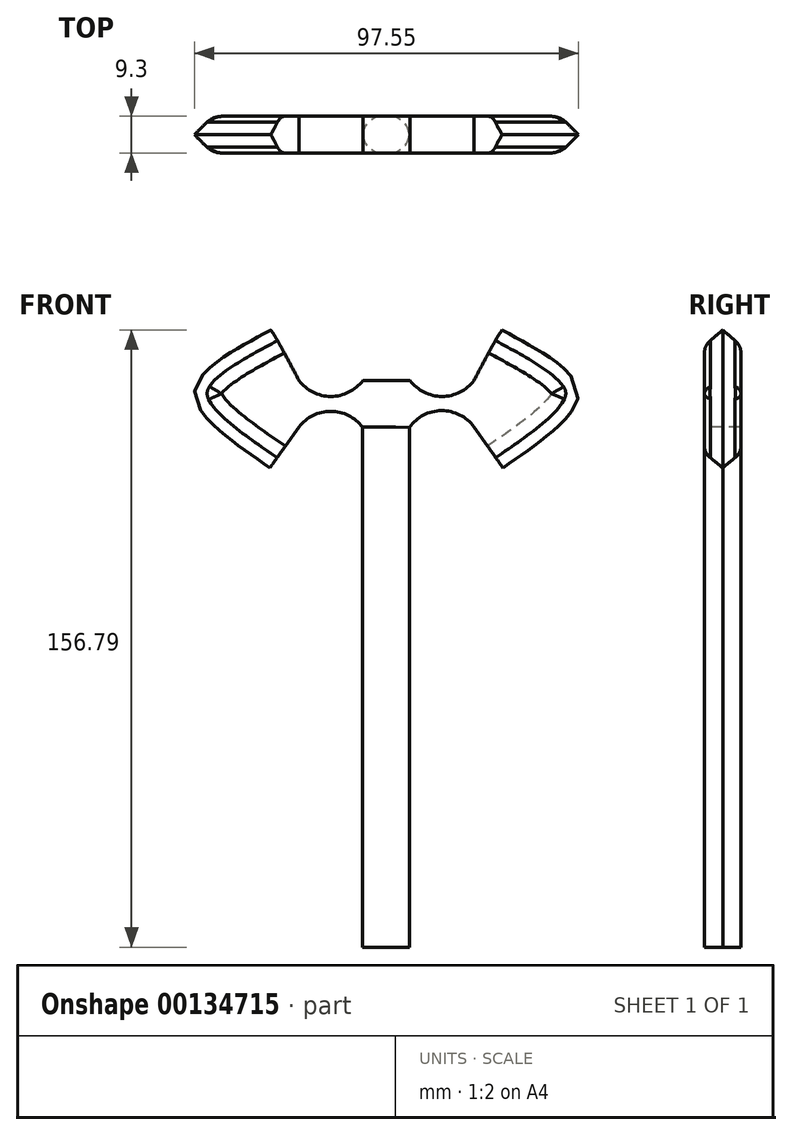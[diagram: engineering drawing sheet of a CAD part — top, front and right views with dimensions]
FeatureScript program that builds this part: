
annotation { "Feature Type Name" : "Feature", "Feature Type Description" : "" }
export const myFeature = defineFeature(function(context is Context, id is Id, definition is map)
    precondition{}
    {
        {
            var Q0;
            Q0=qCreatedBy(makeId("Front.planeOp"),FACE);
            var sketch = newSketch(context, id + "F0", { "sketchPlane" : qUnion([Q0])});
            skLineSegment(sketch, "E0", {"start": v(-59.33, 62.86) * mm, "end": v(-59.33, -69.24) * mm});
            skLineSegment(sketch, "E1", {"start": v(-59.33, -69.24) * mm, "end": v(-47.38, -69.24) * mm});
            skLineSegment(sketch, "E2", {"start": v(-47.38, -69.24) * mm, "end": v(-47.38, 62.86) * mm});
            skLineSegment(sketch, "E3", {"start": v(-47.38, 62.86) * mm, "end": v(-59.33, 62.86) * mm});
            skSolve(sketch);
        }
        {
            var Q0;
            Q0=qCreatedBy(makeId("Front.planeOp"),FACE);
            var sketch = newSketch(context, id + "F1", { "sketchPlane" : qUnion([Q0])});
            skLineSegment(sketch, "E4", {"start": v(-47.22, 74.74) * mm, "end": v(-59.23, 74.74) * mm});
            skLineSegment(sketch, "E5", {"start": v(-59.32, 62.87) * mm, "end": v(-47.4, 62.85) * mm});
            skArc(sketch, "E6", {"start": v(-47.22, 74.74) * mm, "mid": v(-39.1, 70.68) * mm, "end": v(-30.98, 74.74) * mm});
            skPoint(sketch, "E7.startSnap0", {"position": v(-47.22, 68.84) * mm});
            skPoint(sketch, "E7.startSnap1", {"position": v(-53.36, 62.86) * mm});
            skArc(sketch, "E8.MirrorCS", {"start": v(-47.4, 62.85) * mm, "mid": v(-39.21, 67.07) * mm, "end": v(-30.98, 62.95) * mm});
            skPoint(sketch, "E9.endSnap0", {"position": v(-53.22, 74.74) * mm});
            skArc(sketch, "E10.MirrorCS", {"start": v(-59.23, 74.74) * mm, "mid": v(-67.35, 70.68) * mm, "end": v(-75.46, 74.74) * mm});
            skArc(sketch, "E11.MirrorCS", {"start": v(-59.32, 62.87) * mm, "mid": v(-67.37, 66.9) * mm, "end": v(-75.46, 62.95) * mm});
            skFitSpline(sketch, "E12", {"points": [v(-30.98, 74.74) * mm, v(-23.6, 87.78) * mm, v(-23.37, 87.78) * mm], "startDerivative": vector(11.07, 21.16) * mm, "endDerivative": vector(1.7, -0.8) * mm});
            skFitSpline(sketch, "E13", {"points": [v(-23.37, 87.78) * mm, v(-4.02, 71.77) * mm, v(-23.37, 52.2) * mm], "startDerivative": vector(58.52, -31.43) * mm, "endDerivative": vector(-57.64, -39.67) * mm});
            skFitSpline(sketch, "E14", {"points": [v(-30.98, 62.95) * mm, v(-23.37, 52.2) * mm], "startDerivative": vector(7.6, -10.75) * mm, "endDerivative": vector(7.6, -10.75) * mm});
            skFitSpline(sketch, "E15.MirrorCS", {"points": [v(-75.46, 62.95) * mm, v(-83.07, 52.2) * mm], "startDerivative": vector(-7.6, -10.75) * mm, "endDerivative": vector(-7.6, -10.75) * mm});
            skFitSpline(sketch, "E16.MirrorCS", {"points": [v(-75.46, 74.74) * mm, v(-82.85, 87.78) * mm, v(-83.07, 87.78) * mm], "startDerivative": vector(-11.07, 21.16) * mm, "endDerivative": vector(-1.7, -0.8) * mm});
            skFitSpline(sketch, "E17.MirrorCS", {"points": [v(-83.07, 87.78) * mm, v(-102.42, 71.77) * mm, v(-83.07, 52.2) * mm], "startDerivative": vector(-58.52, -31.43) * mm, "endDerivative": vector(57.64, -39.67) * mm});
            skLineSegment(sketch, "E18", {"start": v(-47.22, 74.74) * mm, "end": v(-47.4, 62.85) * mm});
            skLineSegment(sketch, "E19", {"start": v(-59.23, 74.74) * mm, "end": v(-59.32, 62.87) * mm});
            skSolve(sketch);
        }
        {
            var Q0;
            Q0 = qSketchRegion(id + "F1", true);
            var Q1;
            Q1 = qSketchRegion(id + "F0", true);
            extrude(context, id + "F2", {"entities" : qUnion([Q0, Q1]), "depth" : 9.3 * mm});
        }
        {
            var Q0;
            Q0=makeQuery(id+"F2.opExtrude","CAP_EDGE",EDGE,{"disambiguationData":[OSD([sQuery(id+"F0.wireOp",EDGE,"E0")])],"isStart":false});
            var Q1;
            Q1=makeQuery(id+"F2.opExtrude","CAP_EDGE",EDGE,{"disambiguationData":[OSD([sQuery(id+"F0.wireOp",EDGE,"E2")])],"isStart":false});
            var Q2;
            Q2=makeQuery(id+"F2.opExtrude","CAP_EDGE",EDGE,{"disambiguationData":[OSD([sQuery(id+"F0.wireOp",EDGE,"E2")])],"isStart":true});
            var Q3;
            Q3=makeQuery(id+"F2.opExtrude","CAP_EDGE",EDGE,{"disambiguationData":[OSD([sQuery(id+"F0.wireOp",EDGE,"E0")])],"isStart":true});
            fillet(context, id + "F3", {"entities" : qUnion([Q0, Q1, Q2, Q3]), "radius" : 5.08 * mm, "tangentPropagation" : true, "allowEdgeOverflow" : false});
        }
        {
            var Q0;
            Q0=makeQuery(id+"F2.opExtrude","CAP_EDGE",EDGE,{"disambiguationData":[OSD([sQuery(id+"F1.wireOp",EDGE,"E17.MirrorCS")])],"isStart":true});
            var Q1;
            Q1=makeQuery(id+"F2.opExtrude","CAP_EDGE",EDGE,{"disambiguationData":[OSD([sQuery(id+"F1.wireOp",EDGE,"E17.MirrorCS")])],"isStart":false});
            var Q2;
            Q2=makeQuery(id+"F2.opExtrude","CAP_EDGE",EDGE,{"disambiguationData":[OSD([sQuery(id+"F1.wireOp",EDGE,"E13")])],"isStart":false});
            var Q3;
            Q3=makeQuery(id+"F2.opExtrude","CAP_EDGE",EDGE,{"disambiguationData":[OSD([sQuery(id+"F1.wireOp",EDGE,"E13")])],"isStart":true});
            chamfer(context, id + "F4", {"entities" : qUnion([Q0, Q1, Q2, Q3]), "width" : 5.08 * mm, "tangentPropagation" : true});
        }
        {
            var Q0;
            {var subQ0=sQuery(id+"F1.wireOp",EDGE,"E13");Q0=makeQuery(id+"F4.opChamfer","BLEND_EDGE",EDGE,{"blendedFrom":[makeQuery(id+"F2.opExtrude","CAP_EDGE",EDGE,{"disambiguationData":[OSD([subQ0])],"isStart":true}),makeQuery(id+"F2.opExtrude","CAP_FACE",FACE,{"disambiguationData":[OSD([sQuery(id+"F1.wireOp",EDGE,"E4"),sQuery(id+"F1.wireOp",EDGE,"E5"),sQuery(id+"F1.wireOp",EDGE,"E6"),sQuery(id+"F1.wireOp",EDGE,"E8.MirrorCS"),sQuery(id+"F1.wireOp",EDGE,"E10.MirrorCS"),sQuery(id+"F1.wireOp",EDGE,"E11.MirrorCS"),sQuery(id+"F1.wireOp",EDGE,"E12"),subQ0,sQuery(id+"F1.wireOp",EDGE,"E14"),sQuery(id+"F1.wireOp",EDGE,"E15.MirrorCS"),sQuery(id+"F1.wireOp",EDGE,"E16.MirrorCS"),sQuery(id+"F1.wireOp",EDGE,"E17.MirrorCS")])],"isStart":true})],"blendedInto":[makeQuery(id+"F2.opExtrude","CAP_FACE",FACE,{"disambiguationData":[OSD([sQuery(id+"F1.wireOp",EDGE,"E4"),sQuery(id+"F1.wireOp",EDGE,"E5"),sQuery(id+"F1.wireOp",EDGE,"E6"),sQuery(id+"F1.wireOp",EDGE,"E8.MirrorCS"),sQuery(id+"F1.wireOp",EDGE,"E10.MirrorCS"),sQuery(id+"F1.wireOp",EDGE,"E11.MirrorCS"),sQuery(id+"F1.wireOp",EDGE,"E12"),subQ0,sQuery(id+"F1.wireOp",EDGE,"E14"),sQuery(id+"F1.wireOp",EDGE,"E15.MirrorCS"),sQuery(id+"F1.wireOp",EDGE,"E16.MirrorCS"),sQuery(id+"F1.wireOp",EDGE,"E17.MirrorCS")])],"isStart":true})]});}
            var Q1;
            {var subQ0=sQuery(id+"F1.wireOp",EDGE,"E17.MirrorCS");Q1=makeQuery(id+"F4.opChamfer","BLEND_EDGE",EDGE,{"blendedFrom":[makeQuery(id+"F2.opExtrude","CAP_EDGE",EDGE,{"disambiguationData":[OSD([subQ0])],"isStart":true}),makeQuery(id+"F2.opExtrude","CAP_FACE",FACE,{"disambiguationData":[OSD([sQuery(id+"F1.wireOp",EDGE,"E4"),sQuery(id+"F1.wireOp",EDGE,"E5"),sQuery(id+"F1.wireOp",EDGE,"E6"),sQuery(id+"F1.wireOp",EDGE,"E8.MirrorCS"),sQuery(id+"F1.wireOp",EDGE,"E10.MirrorCS"),sQuery(id+"F1.wireOp",EDGE,"E11.MirrorCS"),sQuery(id+"F1.wireOp",EDGE,"E12"),sQuery(id+"F1.wireOp",EDGE,"E13"),sQuery(id+"F1.wireOp",EDGE,"E14"),sQuery(id+"F1.wireOp",EDGE,"E15.MirrorCS"),sQuery(id+"F1.wireOp",EDGE,"E16.MirrorCS"),subQ0])],"isStart":true})],"blendedInto":[makeQuery(id+"F2.opExtrude","CAP_FACE",FACE,{"disambiguationData":[OSD([sQuery(id+"F1.wireOp",EDGE,"E4"),sQuery(id+"F1.wireOp",EDGE,"E5"),sQuery(id+"F1.wireOp",EDGE,"E6"),sQuery(id+"F1.wireOp",EDGE,"E8.MirrorCS"),sQuery(id+"F1.wireOp",EDGE,"E10.MirrorCS"),sQuery(id+"F1.wireOp",EDGE,"E11.MirrorCS"),sQuery(id+"F1.wireOp",EDGE,"E12"),sQuery(id+"F1.wireOp",EDGE,"E13"),sQuery(id+"F1.wireOp",EDGE,"E14"),sQuery(id+"F1.wireOp",EDGE,"E15.MirrorCS"),sQuery(id+"F1.wireOp",EDGE,"E16.MirrorCS"),subQ0])],"isStart":true})]});}
            var Q2;
            {var subQ0=sQuery(id+"F1.wireOp",EDGE,"E13");Q2=makeQuery(id+"F4.opChamfer","BLEND_EDGE",EDGE,{"blendedFrom":[makeQuery(id+"F2.opExtrude","CAP_EDGE",EDGE,{"disambiguationData":[OSD([subQ0])],"isStart":false}),makeQuery(id+"F2.opExtrude","CAP_FACE",FACE,{"disambiguationData":[OSD([sQuery(id+"F1.wireOp",EDGE,"E4"),sQuery(id+"F1.wireOp",EDGE,"E5"),sQuery(id+"F1.wireOp",EDGE,"E6"),sQuery(id+"F1.wireOp",EDGE,"E8.MirrorCS"),sQuery(id+"F1.wireOp",EDGE,"E10.MirrorCS"),sQuery(id+"F1.wireOp",EDGE,"E11.MirrorCS"),sQuery(id+"F1.wireOp",EDGE,"E12"),subQ0,sQuery(id+"F1.wireOp",EDGE,"E14"),sQuery(id+"F1.wireOp",EDGE,"E15.MirrorCS"),sQuery(id+"F1.wireOp",EDGE,"E16.MirrorCS"),sQuery(id+"F1.wireOp",EDGE,"E17.MirrorCS")])],"isStart":false})],"blendedInto":[makeQuery(id+"F2.opExtrude","CAP_FACE",FACE,{"disambiguationData":[OSD([sQuery(id+"F1.wireOp",EDGE,"E4"),sQuery(id+"F1.wireOp",EDGE,"E5"),sQuery(id+"F1.wireOp",EDGE,"E6"),sQuery(id+"F1.wireOp",EDGE,"E8.MirrorCS"),sQuery(id+"F1.wireOp",EDGE,"E10.MirrorCS"),sQuery(id+"F1.wireOp",EDGE,"E11.MirrorCS"),sQuery(id+"F1.wireOp",EDGE,"E12"),subQ0,sQuery(id+"F1.wireOp",EDGE,"E14"),sQuery(id+"F1.wireOp",EDGE,"E15.MirrorCS"),sQuery(id+"F1.wireOp",EDGE,"E16.MirrorCS"),sQuery(id+"F1.wireOp",EDGE,"E17.MirrorCS")])],"isStart":false})]});}
            var Q3;
            {var subQ0=sQuery(id+"F1.wireOp",EDGE,"E17.MirrorCS");Q3=makeQuery(id+"F4.opChamfer","BLEND_EDGE",EDGE,{"blendedFrom":[makeQuery(id+"F2.opExtrude","CAP_EDGE",EDGE,{"disambiguationData":[OSD([subQ0])],"isStart":false}),makeQuery(id+"F2.opExtrude","CAP_FACE",FACE,{"disambiguationData":[OSD([sQuery(id+"F1.wireOp",EDGE,"E4"),sQuery(id+"F1.wireOp",EDGE,"E5"),sQuery(id+"F1.wireOp",EDGE,"E6"),sQuery(id+"F1.wireOp",EDGE,"E8.MirrorCS"),sQuery(id+"F1.wireOp",EDGE,"E10.MirrorCS"),sQuery(id+"F1.wireOp",EDGE,"E11.MirrorCS"),sQuery(id+"F1.wireOp",EDGE,"E12"),sQuery(id+"F1.wireOp",EDGE,"E13"),sQuery(id+"F1.wireOp",EDGE,"E14"),sQuery(id+"F1.wireOp",EDGE,"E15.MirrorCS"),sQuery(id+"F1.wireOp",EDGE,"E16.MirrorCS"),subQ0])],"isStart":false})],"blendedInto":[makeQuery(id+"F2.opExtrude","CAP_FACE",FACE,{"disambiguationData":[OSD([sQuery(id+"F1.wireOp",EDGE,"E4"),sQuery(id+"F1.wireOp",EDGE,"E5"),sQuery(id+"F1.wireOp",EDGE,"E6"),sQuery(id+"F1.wireOp",EDGE,"E8.MirrorCS"),sQuery(id+"F1.wireOp",EDGE,"E10.MirrorCS"),sQuery(id+"F1.wireOp",EDGE,"E11.MirrorCS"),sQuery(id+"F1.wireOp",EDGE,"E12"),sQuery(id+"F1.wireOp",EDGE,"E13"),sQuery(id+"F1.wireOp",EDGE,"E14"),sQuery(id+"F1.wireOp",EDGE,"E15.MirrorCS"),sQuery(id+"F1.wireOp",EDGE,"E16.MirrorCS"),subQ0])],"isStart":false})]});}
            fillet(context, id + "F5", {"entities" : qUnion([Q0, Q1, Q2, Q3]), "radius" : 5.08 * mm, "tangentPropagation" : true, "allowEdgeOverflow" : false});
        }
    });
